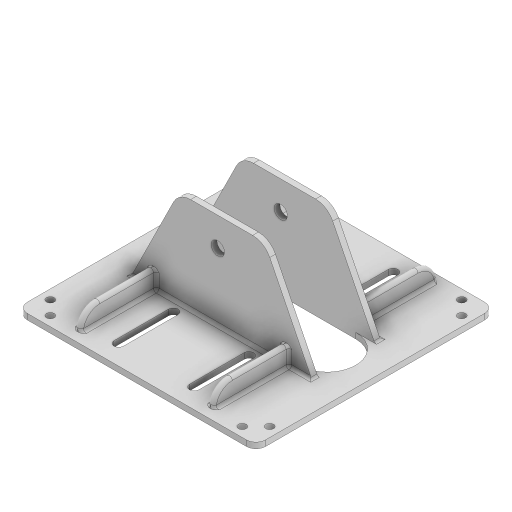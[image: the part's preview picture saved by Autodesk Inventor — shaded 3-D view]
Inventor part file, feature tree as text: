
AUTODESK INVENTOR PART (.ipt)
format: ipt  version: 2023.2 (Build 272271030, 271C)  size: 1,042,432 bytes
history: native  units: mm
features: extrude x8, fillet x5, projected_geometry x5, sketch x2
ambient origin geometry x8: Origin, YZ Plane, XZ Plane, XY Plane, X Axis, Y Axis, Z Axis, Center Point
bodies: Solid1 (feature_tree)
feature tree (20):
  extrude  "Extrusion1"  Depth=120.0mm
  sketch  "Sketch3"  dims[d0=120.0mm d1=120.0mm]
  extrude  "Extrusion2"  Depth=3.0mm
  extrude  "Extrusion4"  Depth=1.5mm
  extrude  "Extrusion5"  Depth=1.5mm
  extrude  "Extrusion6"  Depth=1.5mm TaperAngle=0.0deg
  fillet  "Fillet1"  Radius=50.0mm
  extrude  "Extrusion8"  Depth=1.5mm TaperAngle=0.0deg
  fillet  "Fillet3"  Radius=10.0mm
  fillet  "Fillet4"  Radius=10.0mm
  extrude  "Extrusion12"  Depth=1.5mm
  extrude  "Extrusion13"  Depth=1.5mm
  fillet  "Fillet7"  Radius=100.0mm
  fillet  "Fillet8"  Radius=5.0mm
  projected_geometry  "Projected Loop1"
  projected_geometry  "Projected Loop3"
  projected_geometry  "Projected Loop5"
  projected_geometry  "Projected Loop9"
  sketch  "Sketch22"  dims[d4=3.0mm d5=0.0mm d6=3.0mm d12=5.0mm d14=3.5mm d15=10.0mm d16=0.0mm d20=50.0mm d21=0.0mm d22=50.0mm d23=0.0mm d24=10.0mm d25=0.0mm d26=10.0mm d31=4.1mm d33=4.1mm d35=100.0mm d36=0.0mm d37=5.0mm d41=3.0mm d43=3.0mm d45=3.0mm d46=10.0mm d54=7.0mm d55=100.0mm d56=0.0mm d59=30.0mm d62=125.0mm d63=125.0mm d64=3.0mm d65=0.0mm d66=5.0mm d67=4.1mm d68=4.1mm d69=4.1mm d70=4.1mm d71=4.1mm d72=4.1mm d75=3.0mm d76=3.0mm d77=1.5mm]
  projected_geometry  "Projected Loop10"
